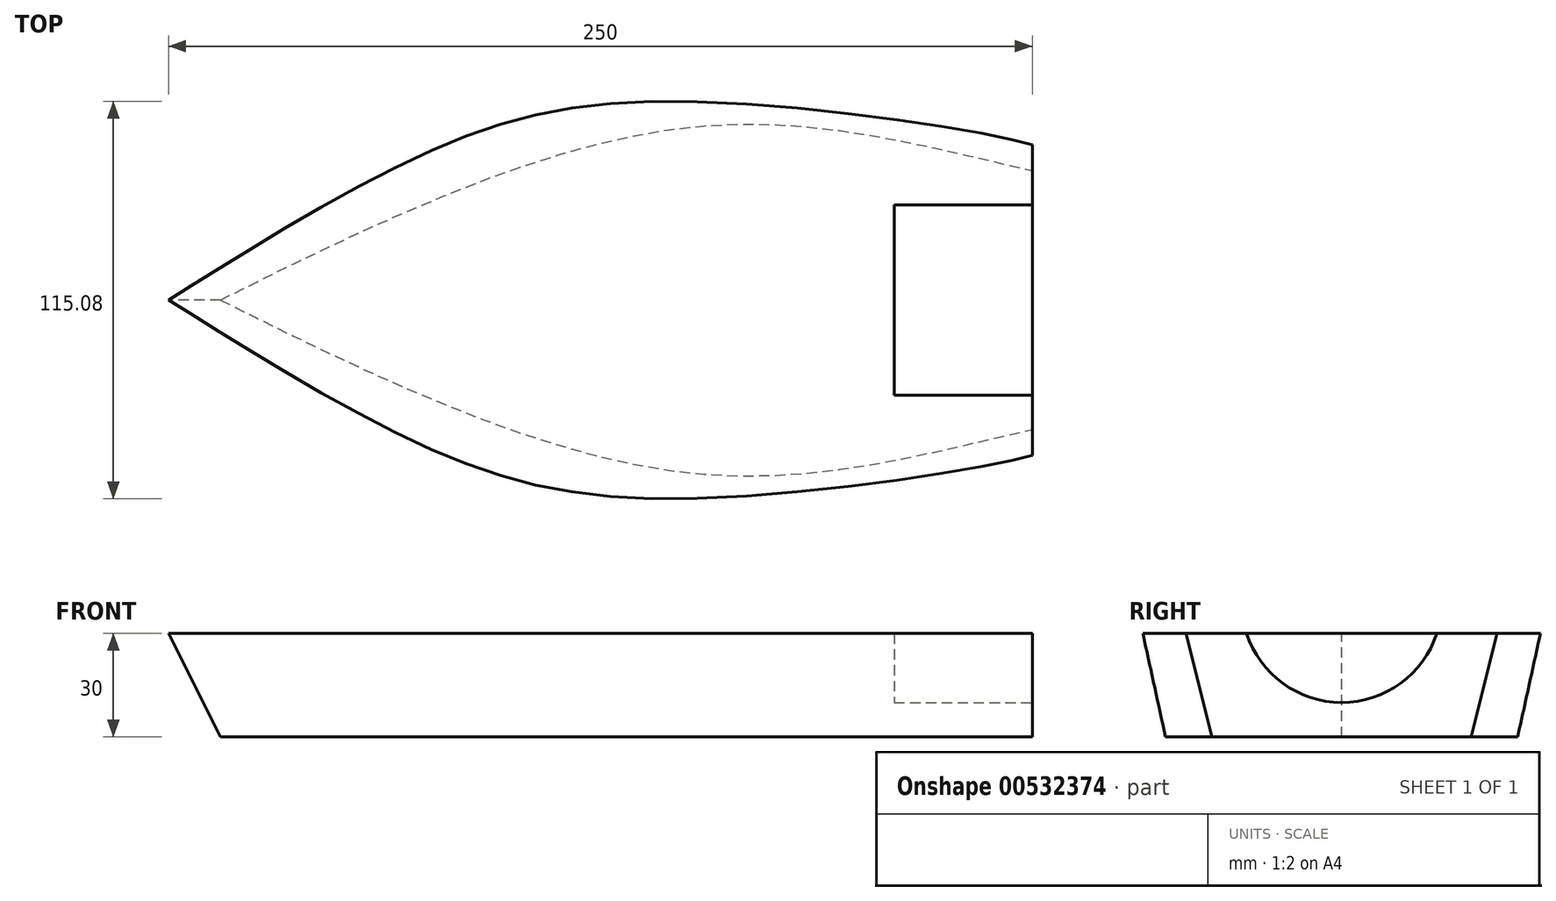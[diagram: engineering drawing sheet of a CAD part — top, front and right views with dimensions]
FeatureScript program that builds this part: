
annotation { "Feature Type Name" : "Feature", "Feature Type Description" : "" }
export const myFeature = defineFeature(function(context is Context, id is Id, definition is map)
    precondition{}
    {
        {
            var Q0;
            Q0=qCreatedBy(makeId("Top.planeOp"),FACE);
            var sketch = newSketch(context, id + "F0", { "sketchPlane" : qUnion([Q0])});
            skLineSegment(sketch, "E0", {"start": v(0, 0) * mm, "end": v(-87.75, 0) * mm, "construction": true});
            skLineSegment(sketch, "E1", {"start": v(0, 0) * mm, "end": v(124.81, 0) * mm, "construction": true});
            skLineSegment(sketch, "E2", {"start": v(162.25, 0) * mm, "end": v(162.25, 45) * mm});
            skFitSpline(sketch, "E3", {"points": [v(162.25, 45) * mm, v(62.25, 57.5) * mm, v(-18.8, 40) * mm, v(-87.75, 0) * mm], "startDerivative": vector(-101.31, 30.98) * mm, "endDerivative": vector(-131.59, -82.95) * mm});
            skLineSegment(sketch, "E4", {"start": v(-87.75, 0) * mm, "end": v(162.25, 0) * mm, "construction": true});
            skFitSpline(sketch, "E5.MirrorCS", {"points": [v(162.25, -45) * mm, v(62.25, -57.5) * mm, v(-18.8, -40) * mm, v(-87.75, 0) * mm], "startDerivative": vector(-101.31, -30.98) * mm, "endDerivative": vector(-131.59, 82.95) * mm});
            skLineSegment(sketch, "E6.MirrorCS", {"start": v(162.25, 0) * mm, "end": v(162.25, -45) * mm});
            skSolve(sketch);
        }
        {
            var Q0;
            Q0=qCreatedBy(makeId("Top.planeOp"),FACE);
            cPlane(context, id + "F1", {"entities" : qUnion([Q0]), "cplaneType" : CPlaneType.OFFSET, "offset" : 30 * mm, "oppositeDirection" : true, "width" : 150 * mm, "height" : 150 * mm});
        }
        {
            var Q0;
            Q0=qCreatedBy(id+"F1.planeOp",FACE);
            var sketch = newSketch(context, id + "F2", { "sketchPlane" : qUnion([Q0])});
            skPoint(sketch, "E7.0", {"position": v(162.25, 0) * mm});
            skPoint(sketch, "E8.0", {"position": v(-87.75, 0) * mm});
            skLineSegment(sketch, "E9", {"start": v(162.25, 0) * mm, "end": v(162.25, 37.5) * mm});
            skFitSpline(sketch, "E10", {"points": [v(-72.75, 0) * mm, v(62.25, 50) * mm, v(162.25, 37.5) * mm], "startDerivative": vector(238.24, 119.4) * mm, "endDerivative": vector(212.55, -48.3) * mm});
            skFitSpline(sketch, "E11.MirrorCS", {"points": [v(-72.75, 0) * mm, v(62.25, -50) * mm, v(162.25, -37.5) * mm], "startDerivative": vector(238.24, -119.4) * mm, "endDerivative": vector(212.55, 48.3) * mm});
            skLineSegment(sketch, "E12.MirrorCS", {"start": v(162.25, 0) * mm, "end": v(162.25, -37.5) * mm});
            skSolve(sketch);
        }
        {
            var Q0;
            Q0=makeQuery(id+"F2.imprint","IMPRINT",FACE,{"disambiguationData":[TD([[makeQuery(id+"F2.imprint","IMPRINT",EDGE,{"derivedFrom":sQuery(id+"F2.wireOp",EDGE,"E9")}),1.0]])]});
            var Q1;
            Q1=makeQuery(id+"F0.imprint","IMPRINT",FACE,{"disambiguationData":[TD([[makeQuery(id+"F0.imprint","IMPRINT",EDGE,{"derivedFrom":sQuery(id+"F0.wireOp",EDGE,"E2")}),1.0]])]});
            loft(context, id + "F3", {"sheetProfilesArray" : [{ "sheetProfileEntities" : qUnion([Q0]) }, { "sheetProfileEntities" : qUnion([Q1]) }]});
        }
        {
            var Q0;
            Q0=makeQuery(id+"F3.opLoft","SWEPT_FACE",FACE,{"disambiguationData":[OSD([sQuery(id+"F0.wireOp",EDGE,"E2"),sQuery(id+"F0.wireOp",EDGE,"E5.MirrorCS"),sQuery(id+"F0.wireOp",EDGE,"E6.MirrorCS"),sQuery(id+"F2.wireOp",EDGE,"E9"),sQuery(id+"F2.wireOp",EDGE,"E11.MirrorCS"),sQuery(id+"F2.wireOp",EDGE,"E12.MirrorCS")])]});
            var sketch = newSketch(context, id + "F4", { "sketchPlane" : qUnion([Q0])});
            skCircle(sketch, "E13", {"center": v(0, 9) * mm, "radius": 29 * mm});
            skSolve(sketch);
        }
        {
            var Q0;
            {var subQ0=sQuery(id+"F4.wireOp",EDGE,"E13");var subQ1=makeQuery(id+"F3.opLoft","MID_CAP_EDGE",EDGE,{"disambiguationData":[OSD([sQuery(id+"F0.wireOp",EDGE,"E2"),sQuery(id+"F0.wireOp",EDGE,"E5.MirrorCS"),sQuery(id+"F0.wireOp",EDGE,"E6.MirrorCS")])],"capPos":1.0});var subQ2=makeQuery(id+"F4.imprint","INTERSECT",VERTEX,{"disambiguationData":[OD(0.0)],"derivedFrom":[subQ1,subQ0]});Q0=makeQuery(id+"F4.imprint","IMPRINT",FACE,{"disambiguationData":[TD([[makeQuery(id+"F4.imprint","IMPRINT",EDGE,{"disambiguationData":[TD([[subQ2,1.0]])],"derivedFrom":subQ0}),1.0]])]});}
            extrude(context, id + "F5", {"entities" : qUnion([Q0]), "operationType" : NewBodyOperationType.REMOVE, "oppositeDirection" : true, "depth" : 40 * mm, "offsetDistance" : 25 * mm});
        }
    });
